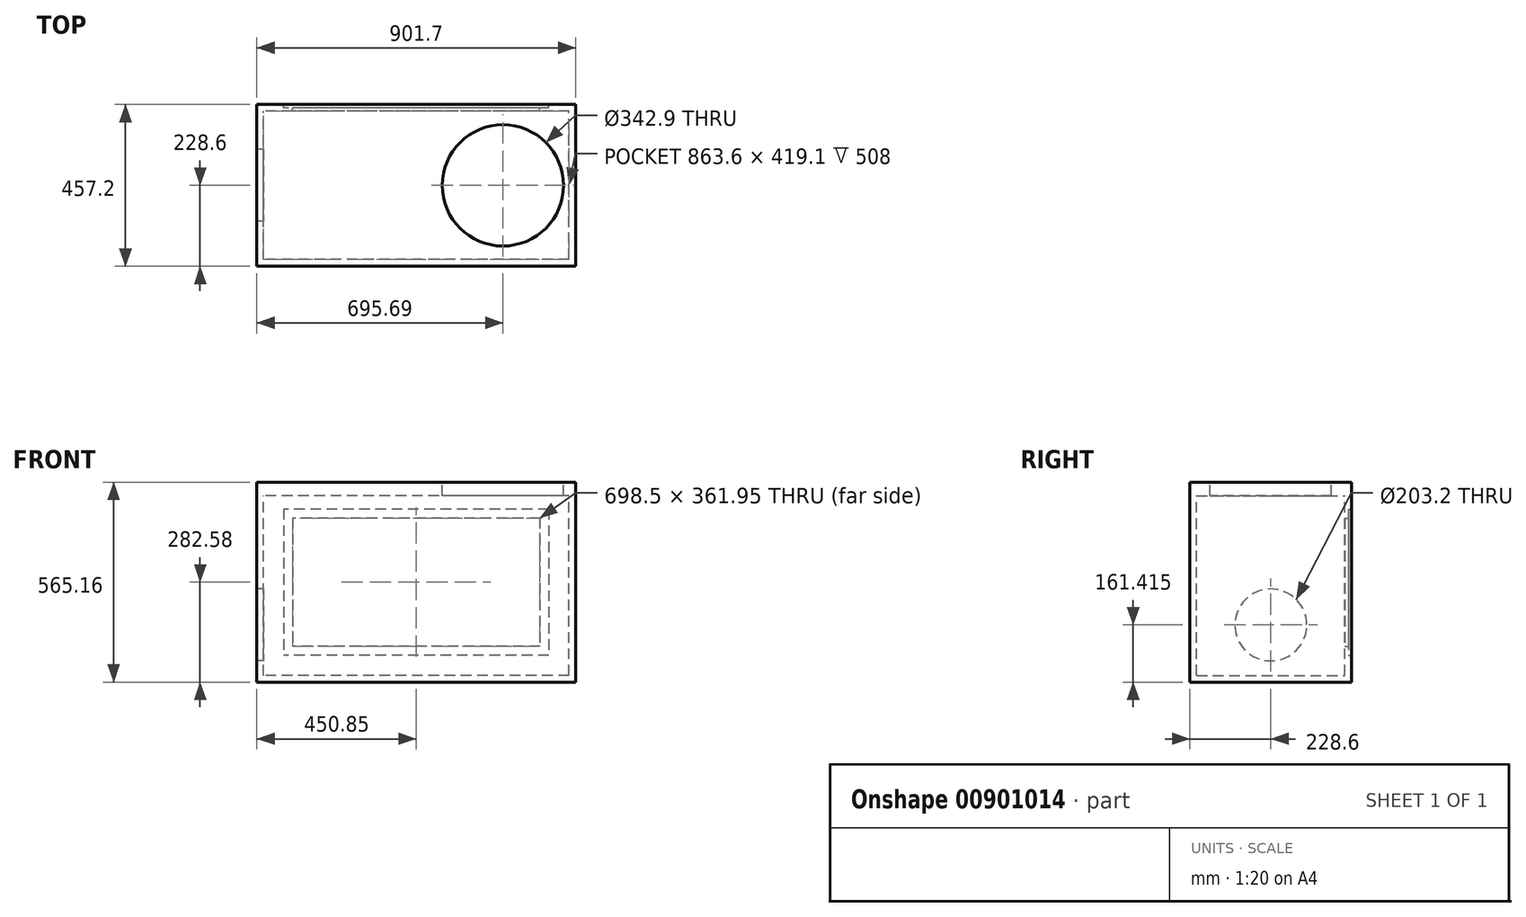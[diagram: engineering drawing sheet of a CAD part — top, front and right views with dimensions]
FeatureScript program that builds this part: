
annotation { "Feature Type Name" : "Feature", "Feature Type Description" : "" }
export const myFeature = defineFeature(function(context is Context, id is Id, definition is map)
    precondition{}
    {
        {
            var Q0;
            Q0=qCreatedBy(makeId("Front.planeOp"),FACE);
            var sketch = newSketch(context, id + "F0", { "sketchPlane" : qUnion([Q0])});
            skLineSegment(sketch, "E0.bottom", {"start": v(450.85, -263.52) * mm, "end": v(-450.85, -263.53) * mm});
            skLineSegment(sketch, "E0.top", {"start": v(450.85, 263.53) * mm, "end": v(-450.85, 263.52) * mm});
            skLineSegment(sketch, "E0.left", {"start": v(450.85, -263.52) * mm, "end": v(450.85, 263.53) * mm});
            skLineSegment(sketch, "E0.right", {"start": v(-450.85, -263.53) * mm, "end": v(-450.85, 263.52) * mm});
            skPoint(sketch, "E0.middle", {"position": v(0, 0) * mm});
            skSolve(sketch);
        }
        {
            var Q0;
            Q0=makeQuery(id+"F0.imprint","IMPRINT",FACE,{"disambiguationData":[TD([[makeQuery(id+"F0.imprint","IMPRINT",EDGE,{"derivedFrom":sQuery(id+"F0.wireOp",EDGE,"E0.bottom")}),-1.0]])]});
            extrude(context, id + "F1", {"entities" : qUnion([Q0]), "depth" : 457.2 * mm, "offsetDistance" : 25.4 * mm});
        }
        {
            var Q0;
            Q0=makeQuery(id+"F1.opExtrude","SWEPT_FACE",FACE,{"disambiguationData":[OSD([sQuery(id+"F0.wireOp",EDGE,"E0.top")])]});
            shell(context, id + "F2", {"entities" : qUnion([Q0]), "thickness" : 19.05 * mm});
        }
        {
            var Q0;
            Q0=makeQuery(id+"F1.opExtrude","SWEPT_FACE",FACE,{"disambiguationData":[OSD([sQuery(id+"F0.wireOp",EDGE,"E0.top")])]});
            var sketch = newSketch(context, id + "F3", { "sketchPlane" : qUnion([Q0])});
            skLineSegment(sketch, "E1.bottom", {"start": v(-450.85, 0) * mm, "end": v(450.85, 0) * mm});
            skLineSegment(sketch, "E1.top", {"start": v(-450.85, -457.2) * mm, "end": v(450.85, -457.2) * mm});
            skLineSegment(sketch, "E1.left", {"start": v(-450.85, 0) * mm, "end": v(-450.85, -457.2) * mm});
            skLineSegment(sketch, "E1.right", {"start": v(450.85, 0) * mm, "end": v(450.85, -457.2) * mm});
            skSolve(sketch);
        }
        {
            var Q0;
            Q0 = qSketchRegion(id + "F3", true);
            extrude(context, id + "F4", {"entities" : qUnion([Q0]), "operationType" : NewBodyOperationType.ADD, "depth" : 38.1 * mm, "offsetDistance" : 25.4 * mm});
        }
        {
            var Q0;
            Q0=makeQuery(id+"F4.boolean.opBoolean","MERGE",FACE,{"derivedFrom":[makeQuery(id+"F1.opExtrude","SWEPT_FACE",FACE,{"disambiguationData":[OSD([sQuery(id+"F0.wireOp",EDGE,"E0.right")])]}),makeQuery(id+"F4.opExtrude","SWEPT_FACE",FACE,{"disambiguationData":[OSD([sQuery(id+"F3.wireOp",EDGE,"E1.left")])]})]});
            var sketch = newSketch(context, id + "F5", { "sketchPlane" : qUnion([Q0])});
            skCircle(sketch, "E2", {"center": v(228.6, -102.12) * mm, "radius": 101.6 * mm});
            skPoint(sketch, "E2.centerSnap0", {"position": v(228.6, -263.53) * mm});
            skSolve(sketch);
        }
        {
            var Q0;
            Q0=makeQuery(id+"F5.imprint","IMPRINT",FACE,{"disambiguationData":[TD([[makeQuery(id+"F5.imprint","IMPRINT",EDGE,{"derivedFrom":sQuery(id+"F5.wireOp",EDGE,"E2")}),1.0]])]});
            extrude(context, id + "F6", {"entities" : qUnion([Q0]), "operationType" : NewBodyOperationType.REMOVE, "endBound" : BoundingType.UP_TO_NEXT, "oppositeDirection" : true, "depth" : 25.4 * mm, "offsetDistance" : 25.4 * mm});
        }
        {
            var Q0;
            Q0=makeQuery(id+"F4.opExtrude","CAP_FACE",FACE,{"disambiguationData":[OSD([sQuery(id+"F3.wireOp",EDGE,"E1.bottom"),sQuery(id+"F3.wireOp",EDGE,"E1.top"),sQuery(id+"F3.wireOp",EDGE,"E1.left"),sQuery(id+"F3.wireOp",EDGE,"E1.right")])],"isStart":false});
            var sketch = newSketch(context, id + "F7", { "sketchPlane" : qUnion([Q0])});
            skCircle(sketch, "E3", {"center": v(244.84, -228.6) * mm, "radius": 171.45 * mm});
            skPoint(sketch, "E3.centerSnap0", {"position": v(450.85, -228.6) * mm});
            skSolve(sketch);
        }
        {
            var Q0;
            Q0=makeQuery(id+"F7.imprint","IMPRINT",FACE,{"disambiguationData":[TD([[makeQuery(id+"F7.imprint","IMPRINT",EDGE,{"derivedFrom":sQuery(id+"F7.wireOp",EDGE,"E3")}),1.0]])]});
            extrude(context, id + "F8", {"entities" : qUnion([Q0]), "operationType" : NewBodyOperationType.REMOVE, "endBound" : BoundingType.UP_TO_NEXT, "oppositeDirection" : true, "depth" : 25.4 * mm, "offsetDistance" : 25.4 * mm});
        }
        {
            var Q0;
            Q0=makeQuery(id+"F4.boolean.opBoolean","MERGE",FACE,{"derivedFrom":[makeQuery(id+"F1.opExtrude","CAP_FACE",FACE,{"disambiguationData":[OSD([sQuery(id+"F0.wireOp",EDGE,"E0.bottom"),sQuery(id+"F0.wireOp",EDGE,"E0.top"),sQuery(id+"F0.wireOp",EDGE,"E0.left"),sQuery(id+"F0.wireOp",EDGE,"E0.right")])],"isStart":true}),makeQuery(id+"F4.opExtrude","SWEPT_FACE",FACE,{"disambiguationData":[OSD([sQuery(id+"F3.wireOp",EDGE,"E1.bottom")])]})]});
            var sketch = newSketch(context, id + "F9", { "sketchPlane" : qUnion([Q0])});
            skLineSegment(sketch, "E4.bottom", {"start": v(-374.65, 225.43) * mm, "end": v(374.65, 225.43) * mm});
            skLineSegment(sketch, "E4.top", {"start": v(-374.65, -187.33) * mm, "end": v(374.65, -187.33) * mm});
            skLineSegment(sketch, "E4.left", {"start": v(-374.65, 225.43) * mm, "end": v(-374.65, -187.33) * mm});
            skLineSegment(sketch, "E4.right", {"start": v(374.65, 225.43) * mm, "end": v(374.65, -187.33) * mm});
            skSolve(sketch);
        }
        {
            var Q0;
            Q0=makeQuery(id+"F9.imprint","IMPRINT",FACE,{"disambiguationData":[TD([[makeQuery(id+"F9.imprint","IMPRINT",EDGE,{"derivedFrom":sQuery(id+"F9.wireOp",EDGE,"E4.bottom")}),-1.0]])]});
            extrude(context, id + "F10", {"entities" : qUnion([Q0]), "operationType" : NewBodyOperationType.REMOVE, "oppositeDirection" : true, "depth" : 9.52 * mm, "offsetDistance" : 25.4 * mm});
        }
        {
            var Q0;
            Q0=makeQuery(id+"F10.boolean.opBoolean","COPY",FACE,{"derivedFrom":makeQuery(id+"F10.opExtrude","CAP_FACE",FACE,{"disambiguationData":[OSD([sQuery(id+"F9.wireOp",EDGE,"E4.bottom"),sQuery(id+"F9.wireOp",EDGE,"E4.top"),sQuery(id+"F9.wireOp",EDGE,"E4.left"),sQuery(id+"F9.wireOp",EDGE,"E4.right")])],"isStart":false})});
            var sketch = newSketch(context, id + "F11", { "sketchPlane" : qUnion([Q0])});
            skLineSegment(sketch, "E5.bottom", {"start": v(-349.25, 200.03) * mm, "end": v(349.25, 200.03) * mm});
            skLineSegment(sketch, "E5.top", {"start": v(-349.25, -161.93) * mm, "end": v(349.25, -161.93) * mm});
            skLineSegment(sketch, "E5.left", {"start": v(-349.25, 200.03) * mm, "end": v(-349.25, -161.93) * mm});
            skLineSegment(sketch, "E5.right", {"start": v(349.25, 200.03) * mm, "end": v(349.25, -161.93) * mm});
            skSolve(sketch);
        }
        {
            var Q0;
            Q0 = qSketchRegion(id + "F11", true);
            extrude(context, id + "F12", {"entities" : qUnion([Q0]), "operationType" : NewBodyOperationType.REMOVE, "endBound" : BoundingType.UP_TO_NEXT, "oppositeDirection" : true, "depth" : 25.4 * mm, "offsetDistance" : 25.4 * mm});
        }
    });
